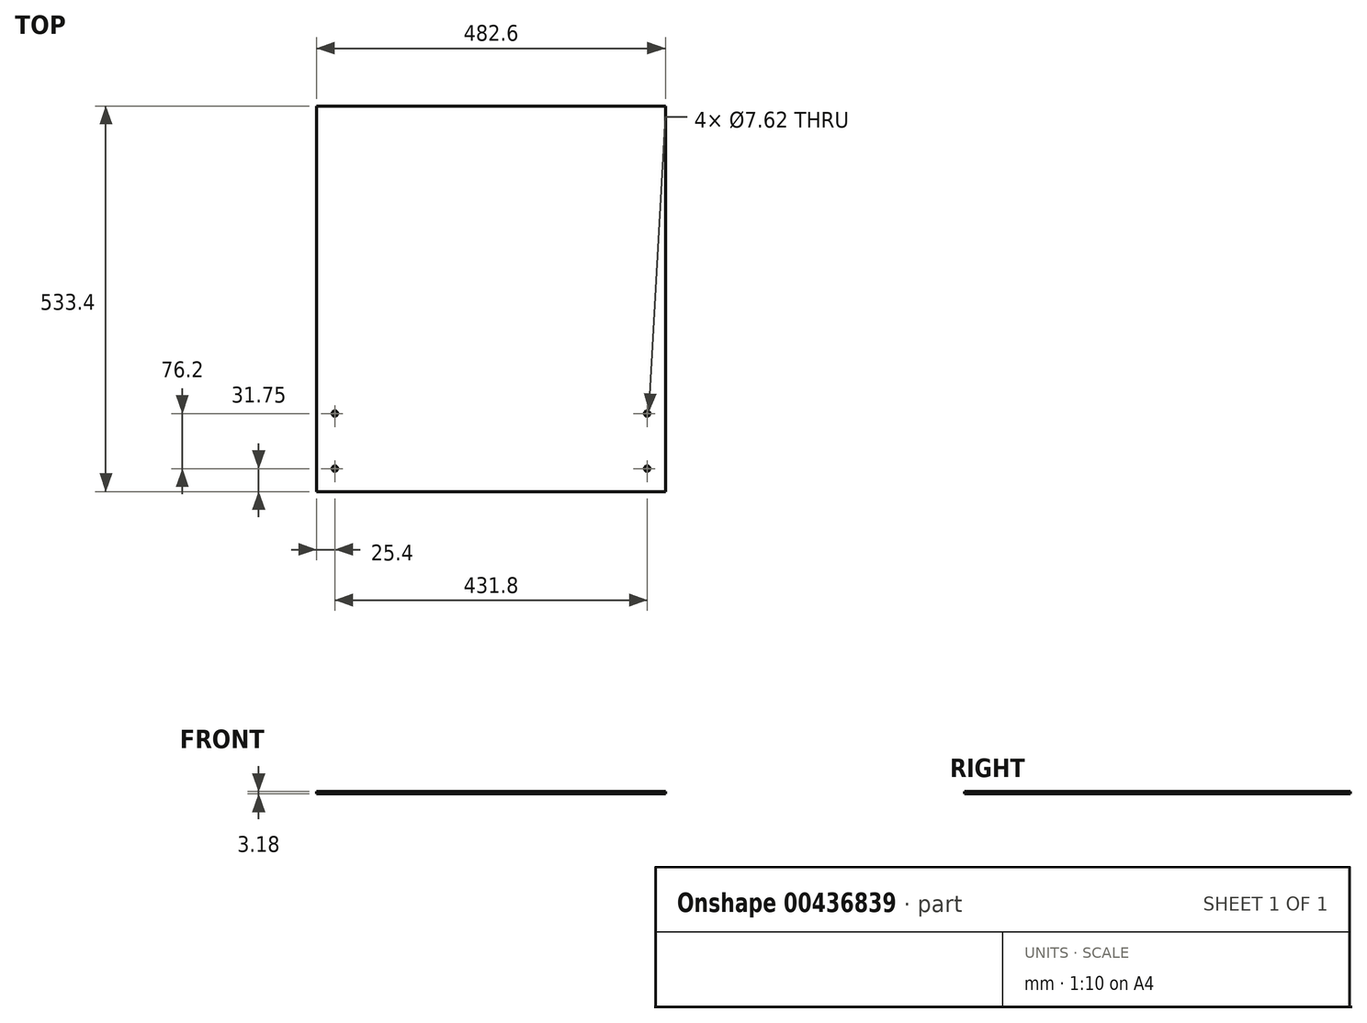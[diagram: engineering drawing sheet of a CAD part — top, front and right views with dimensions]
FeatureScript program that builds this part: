
annotation { "Feature Type Name" : "Feature", "Feature Type Description" : "" }
export const myFeature = defineFeature(function(context is Context, id is Id, definition is map)
    precondition{}
    {
        {
            var Q0;
            Q0=qCreatedBy(makeId("Top.planeOp"),FACE);
            var sketch = newSketch(context, id + "F0", { "sketchPlane" : qUnion([Q0])});
            skLineSegment(sketch, "E0.bottom", {"start": v(0, 0) * mm, "end": v(482.6, 0) * mm});
            skLineSegment(sketch, "E0.top", {"start": v(0, -533.4) * mm, "end": v(482.6, -533.4) * mm});
            skLineSegment(sketch, "E0.left", {"start": v(0, 0) * mm, "end": v(0, -533.4) * mm});
            skLineSegment(sketch, "E0.right", {"start": v(482.6, 0) * mm, "end": v(482.6, -533.4) * mm});
            skSolve(sketch);
        }
        {
            var Q0;
            Q0=makeQuery(id+"F0.imprint","IMPRINT",FACE,{"disambiguationData":[TD([[makeQuery(id+"F0.imprint","IMPRINT",EDGE,{"derivedFrom":sQuery(id+"F0.wireOp",EDGE,"E0.bottom")}),-1.0]])]});
            var Q1;
            Q1=sQuery(id+"F0.wireOp",EDGE,"E0.top");
            var Q2;
            Q2=sQuery(id+"F0.wireOp",EDGE,"E0.left");
            var Q3;
            Q3=sQuery(id+"F0.wireOp",EDGE,"E0.bottom");
            var Q4;
            Q4=sQuery(id+"F0.wireOp",EDGE,"E0.right");
            extrude(context, id + "F1", {"entities" : qUnion([Q0]), "surfaceEntities" : qUnion([Q1, Q2, Q3, Q4]), "oppositeDirection" : true, "depth" : 3.17 * mm, "offsetDistance" : 25.4 * mm});
        }
        {
            var Q0;
            Q0=makeQuery(id+"F0.imprint","IMPRINT",FACE,{"disambiguationData":[TD([[makeQuery(id+"F0.imprint","IMPRINT",EDGE,{"derivedFrom":sQuery(id+"F0.wireOp",EDGE,"E0.bottom")}),-1.0]])]});
            var sketch = newSketch(context, id + "F2", { "sketchPlane" : qUnion([Q0])});
            skCircle(sketch, "E1", {"center": v(25.4, -425.45) * mm, "radius": 3.81 * mm});
            skCircle(sketch, "E2", {"center": v(457.2, -425.45) * mm, "radius": 3.81 * mm});
            skCircle(sketch, "E3", {"center": v(457.2, -501.65) * mm, "radius": 3.81 * mm});
            skCircle(sketch, "E4", {"center": v(25.4, -501.65) * mm, "radius": 3.81 * mm});
            skSolve(sketch);
        }
        {
            var Q0;
            Q0 = qSketchRegion(id + "F2", true);
            var Q1;
            Q1=makeQuery(id+"F1.opExtrude","CAP_FACE",FACE,{"disambiguationData":[OSD([sQuery(id+"F0.wireOp",EDGE,"E0.bottom"),sQuery(id+"F0.wireOp",EDGE,"E0.top"),sQuery(id+"F0.wireOp",EDGE,"E0.left"),sQuery(id+"F0.wireOp",EDGE,"E0.right")])],"isStart":false});
            extrude(context, id + "F3", {"entities" : qUnion([Q0]), "operationType" : NewBodyOperationType.REMOVE, "endBound" : BoundingType.UP_TO_SURFACE, "oppositeDirection" : true, "depth" : 25.4 * mm, "endBoundEntityFace" : qUnion([Q1]), "offsetDistance" : 25.4 * mm});
        }
    });
